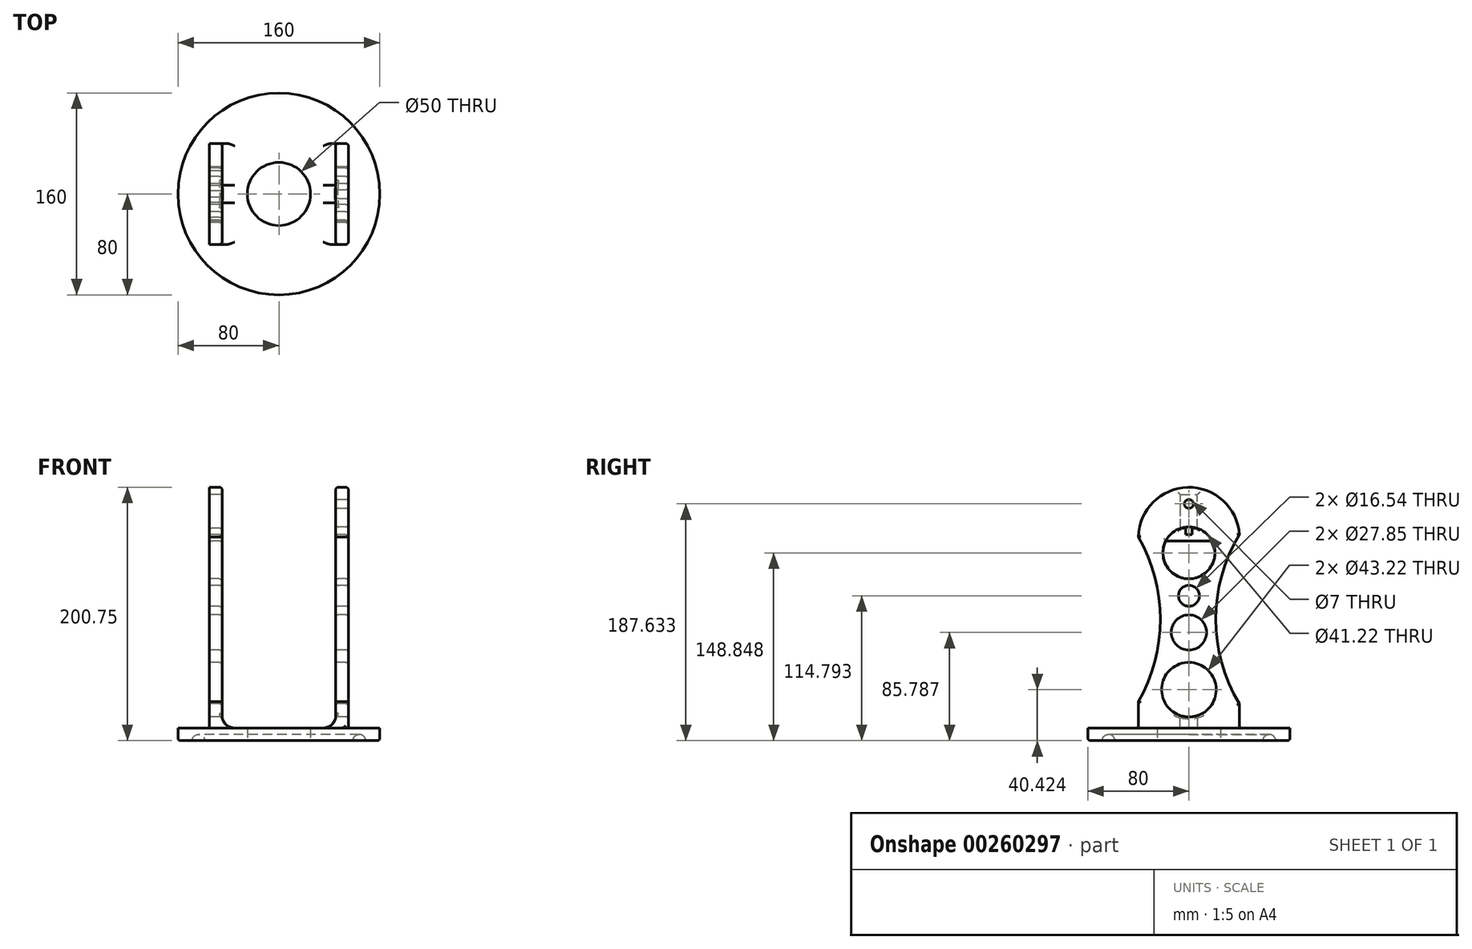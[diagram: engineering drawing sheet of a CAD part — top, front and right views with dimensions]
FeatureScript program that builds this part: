
annotation { "Feature Type Name" : "Feature", "Feature Type Description" : "" }
export const myFeature = defineFeature(function(context is Context, id is Id, definition is map)
    precondition{}
    {
        {
            var Q0;
            Q0=qCreatedBy(makeId("Top.planeOp"),FACE);
            var sketch = newSketch(context, id + "F0", { "sketchPlane" : qUnion([Q0])});
            skCircle(sketch, "E0", {"center": v(0, 0) * mm, "radius": 100 * mm});
            skSolve(sketch);
        }
        {
            var Q0;
            Q0=makeQuery(id+"F0.imprint","IMPRINT",FACE,{"disambiguationData":[TD([[makeQuery(id+"F0.imprint","IMPRINT",EDGE,{"derivedFrom":sQuery(id+"F0.wireOp",EDGE,"E0")}),1.0]])]});
            extrude(context, id + "F1", {"entities" : qUnion([Q0]), "depth" : 10 * mm});
        }
        {
            var Q0;
            Q0=qCreatedBy(makeId("Front.planeOp"),FACE);
            var sketch = newSketch(context, id + "F2", { "sketchPlane" : qUnion([Q0])});
            skCircle(sketch, "E1", {"center": v(-63.7, 0) * mm, "radius": 5 * mm});
            skLineSegment(sketch, "E2", {"start": v(0, 0) * mm, "end": v(-63.7, 0) * mm});
            skSolve(sketch);
        }
        {
            var Q0;
            Q0=makeQuery(id+"F2.imprint","IMPRINT",FACE,{"disambiguationData":[TD([[makeQuery(id+"F2.imprint","IMPRINT",EDGE,{"derivedFrom":sQuery(id+"F2.wireOp",EDGE,"E1")}),1.0]])]});
            var Q1;
            Q1=makeQuery(id+"F1.opExtrude","CAP_EDGE",EDGE,{"disambiguationData":[OSD([sQuery(id+"F0.wireOp",EDGE,"E0")])],"isStart":true});
            revolve(context, id + "F3", {"operationType" : NewBodyOperationType.REMOVE, "entities" : qUnion([Q0]), "axis" : qUnion([Q1]), "revolveType" : RevolveType.FULL, "oppositeDirection" : true});
        }
        {
            var Q0;
            Q0=makeQuery(id+"F1.opExtrude","CAP_FACE",FACE,{"disambiguationData":[OSD([sQuery(id+"F0.wireOp",EDGE,"E0")])],"isStart":false});
            cPlane(context, id + "F4", {"entities" : qUnion([Q0]), "cplaneType" : CPlaneType.OFFSET, "offset" : 0 * mm, "width" : 152.4 * mm, "height" : 152.4 * mm});
        }
        {
            var Q0;
            Q0=makeQuery(id+"F1.opExtrude","CAP_FACE",FACE,{"disambiguationData":[OSD([sQuery(id+"F0.wireOp",EDGE,"E0")])],"isStart":false});
            var sketch = newSketch(context, id + "F5", { "sketchPlane" : qUnion([Q0])});
            skLineSegment(sketch, "E3.bottom", {"start": v(55, 40) * mm, "end": v(-55, 40) * mm});
            skLineSegment(sketch, "E3.top", {"start": v(55, -40) * mm, "end": v(-55, -40) * mm});
            skLineSegment(sketch, "E3.left", {"start": v(55, 40) * mm, "end": v(55, -40) * mm});
            skLineSegment(sketch, "E3.right", {"start": v(-55, 40) * mm, "end": v(-55, -40) * mm});
            skPoint(sketch, "E3.middle", {"position": v(0, 0) * mm});
            skSolve(sketch);
        }
        {
            var Q0;
            Q0=makeQuery(id+"F5.imprint","IMPRINT",FACE,{"disambiguationData":[TD([[makeQuery(id+"F5.imprint","IMPRINT",EDGE,{"derivedFrom":sQuery(id+"F5.wireOp",EDGE,"E3.bottom")}),1.0]])]});
            extrude(context, id + "F6", {"entities" : qUnion([Q0]), "operationType" : NewBodyOperationType.ADD, "depth" : 195 * mm});
        }
        {
            var Q0;
            Q0=makeQuery(id+"F6.opExtrude","CAP_FACE",FACE,{"disambiguationData":[OSD([sQuery(id+"F5.wireOp",EDGE,"E3.bottom"),sQuery(id+"F5.wireOp",EDGE,"E3.top"),sQuery(id+"F5.wireOp",EDGE,"E3.left"),sQuery(id+"F5.wireOp",EDGE,"E3.right")])],"isStart":false});
            var sketch = newSketch(context, id + "F7", { "sketchPlane" : qUnion([Q0])});
            skLineSegment(sketch, "E4.bottom", {"start": v(45, 40) * mm, "end": v(-45, 40) * mm});
            skLineSegment(sketch, "E4.top", {"start": v(45, -40) * mm, "end": v(-45, -40) * mm});
            skLineSegment(sketch, "E4.left", {"start": v(45, 40) * mm, "end": v(45, -40) * mm});
            skLineSegment(sketch, "E4.right", {"start": v(-45, 40) * mm, "end": v(-45, -40) * mm});
            skPoint(sketch, "E4.middle", {"position": v(0, 0) * mm});
            skSolve(sketch);
        }
        {
            var Q0;
            Q0 = qSketchRegion(id + "F7", true);
            extrude(context, id + "F8", {"entities" : qUnion([Q0]), "operationType" : NewBodyOperationType.REMOVE, "oppositeDirection" : true, "depth" : 195 * mm});
        }
        {
            var Q0;
            Q0=qCreatedBy(makeId("Top.planeOp"),FACE);
            var sketch = newSketch(context, id + "F9", { "sketchPlane" : qUnion([Q0])});
            skCircle(sketch, "E5", {"center": v(0, 0) * mm, "radius": 3.75 * mm});
            skSolve(sketch);
        }
        {
            var Q0;
            Q0 = qSketchRegion(id + "F9", true);
            extrude(context, id + "F10", {"entities" : qUnion([Q0]), "operationType" : NewBodyOperationType.REMOVE, "depth" : 12 * mm});
        }
        {
            var Q0;
            Q0=makeQuery(id+"F3.boolean.opBoolean","SPLIT",FACE,{"disambiguationData":[TD([makeQuery(id+"F3.opRevolve","SWEPT_FACE",FACE,{"disambiguationData":[OSD([sQuery(id+"F2.wireOp",EDGE,"E1")])]})])],"derivedFrom":makeQuery(id+"F1.opExtrude","CAP_FACE",FACE,{"disambiguationData":[OSD([sQuery(id+"F0.wireOp",EDGE,"E0")])],"isStart":true})});
            var sketch = newSketch(context, id + "F11", { "sketchPlane" : qUnion([Q0])});
            skCircle(sketch, "E6", {"center": v(0, 0) * mm, "radius": 25 * mm});
            skSolve(sketch);
        }
        {
            var Q0;
            Q0 = qSketchRegion(id + "F11", true);
            extrude(context, id + "F12", {"entities" : qUnion([Q0]), "operationType" : NewBodyOperationType.REMOVE, "oppositeDirection" : true, "depth" : 16 * mm});
        }
        {
            var Q0;
            Q0=makeQuery(id+"F6.opExtrude","SWEPT_FACE",FACE,{"disambiguationData":[OSD([sQuery(id+"F5.wireOp",EDGE,"E3.left")])]});
            var sketch = newSketch(context, id + "F13", { "sketchPlane" : qUnion([Q0])});
            skCircle(sketch, "E7", {"center": v(0, 187.63) * mm, "radius": 3.5 * mm});
            skPoint(sketch, "E7.centerSnap0", {"position": v(0, 195) * mm});
            skSolve(sketch);
        }
        {
            var Q0;
            Q0 = qSketchRegion(id + "F13", true);
            extrude(context, id + "F14", {"entities" : qUnion([Q0]), "operationType" : NewBodyOperationType.REMOVE, "oppositeDirection" : true, "depth" : 123.95 * mm});
        }
        {
            var Q0;
            Q0=makeQuery(id+"F3.boolean.opBoolean","INTERSECT",EDGE,{"disambiguationData":[OD(0.0)],"derivedFrom":[makeQuery(id+"F1.opExtrude","CAP_FACE",FACE,{"disambiguationData":[OSD([sQuery(id+"F0.wireOp",EDGE,"E0")])],"isStart":true}),makeQuery(id+"F3.opRevolve","SWEPT_FACE",FACE,{"disambiguationData":[OSD([sQuery(id+"F2.wireOp",EDGE,"E1")])]})]});
            var Q1;
            Q1=makeQuery(id+"F3.boolean.opBoolean","INTERSECT",EDGE,{"disambiguationData":[OD(1.0)],"derivedFrom":[makeQuery(id+"F1.opExtrude","CAP_FACE",FACE,{"disambiguationData":[OSD([sQuery(id+"F0.wireOp",EDGE,"E0")])],"isStart":true}),makeQuery(id+"F3.opRevolve","SWEPT_FACE",FACE,{"disambiguationData":[OSD([sQuery(id+"F2.wireOp",EDGE,"E1")])]})]});
            fillet(context, id + "F15", {"entities" : qUnion([Q0, Q1]), "radius" : 2 * mm, "tangentPropagation" : true, "allowEdgeOverflow" : false});
        }
        {
            var Q0;
            Q0=makeQuery(id+"F6.opExtrude","SWEPT_FACE",FACE,{"disambiguationData":[OSD([sQuery(id+"F5.wireOp",EDGE,"E3.right")])]});
            var sketch = newSketch(context, id + "F16", { "sketchPlane" : qUnion([Q0])});
            skArc(sketch, "E8", {"start": v(40, 161.53) * mm, "mid": v(0.84, 200.74) * mm, "end": v(-40, 163.27) * mm});
            skArc(sketch, "E9", {"start": v(-40, 29.22) * mm, "mid": v(-21.31, 96.25) * mm, "end": v(-40, 163.27) * mm});
            skArc(sketch, "E10", {"start": v(40, 161.53) * mm, "mid": v(22.68, 96.23) * mm, "end": v(40, 30.93) * mm});
            skSolve(sketch);
        }
        {
            var Q0;
            {var subQ0=sQuery(id+"F16.wireOp",EDGE,"E8");var subQ1=sQuery(id+"F5.wireOp",EDGE,"E3.right");var subQ4=makeQuery(id+"F6.opExtrude","CAP_EDGE",EDGE,{"disambiguationData":[OSD([subQ1])],"isStart":false});var subQ5=makeQuery(id+"F16.imprint","INTERSECT",VERTEX,{"disambiguationData":[OD(1.0)],"derivedFrom":[subQ4,subQ0]});Q0=makeQuery(id+"F16.imprint","IMPRINT",FACE,{"disambiguationData":[TD([[makeQuery(id+"F16.imprint","IMPRINT",EDGE,{"disambiguationData":[TD([[subQ5,1.0]])],"derivedFrom":subQ4}),-1.0]])]});}
            var Q1;
            {var subQ0=sQuery(id+"F16.wireOp",EDGE,"E8");var subQ1=sQuery(id+"F5.wireOp",EDGE,"E3.right");var subQ4=makeQuery(id+"F6.opExtrude","CAP_EDGE",EDGE,{"disambiguationData":[OSD([subQ1])],"isStart":false});var subQ5=makeQuery(id+"F16.imprint","INTERSECT",VERTEX,{"disambiguationData":[OD(0.0)],"derivedFrom":[subQ4,subQ0]});Q1=makeQuery(id+"F16.imprint","IMPRINT",FACE,{"disambiguationData":[TD([[makeQuery(id+"F16.imprint","IMPRINT",EDGE,{"disambiguationData":[TD([[subQ5,-1.0]])],"derivedFrom":subQ4}),-1.0]])]});}
            var Q2;
            {var subQ0=sQuery(id+"F16.wireOp",EDGE,"E10");Q2=makeQuery(id+"F16.imprint","IMPRINT",FACE,{"disambiguationData":[TD([[makeQuery(id+"F16.imprint","IMPRINT",EDGE,{"derivedFrom":subQ0}),1.0]])]});}
            var Q3;
            {var subQ0=sQuery(id+"F16.wireOp",EDGE,"E9");Q3=makeQuery(id+"F16.imprint","IMPRINT",FACE,{"disambiguationData":[TD([[makeQuery(id+"F16.imprint","IMPRINT",EDGE,{"derivedFrom":subQ0}),1.0]])]});}
            extrude(context, id + "F17", {"entities" : qUnion([Q0, Q1, Q2, Q3]), "operationType" : NewBodyOperationType.REMOVE, "oppositeDirection" : true, "depth" : 124.97 * mm});
        }
        {
            var Q0;
            Q0=makeQuery(id+"F6.opExtrude","SWEPT_FACE",FACE,{"disambiguationData":[OSD([sQuery(id+"F5.wireOp",EDGE,"E3.right")])]});
            var sketch = newSketch(context, id + "F18", { "sketchPlane" : qUnion([Q0])});
            skCircle(sketch, "E11", {"center": v(0, 148.85) * mm, "radius": 20.6 * mm});
            skCircle(sketch, "E12", {"center": v(0, 40.42) * mm, "radius": 21.6 * mm});
            skCircle(sketch, "E13", {"center": v(0, 85.79) * mm, "radius": 13.93 * mm});
            skCircle(sketch, "E14", {"center": v(0, 114.8) * mm, "radius": 8.27 * mm});
            skSolve(sketch);
        }
        {
            var Q0;
            Q0 = qSketchRegion(id + "F18", true);
            extrude(context, id + "F19", {"entities" : qUnion([Q0]), "operationType" : NewBodyOperationType.REMOVE, "oppositeDirection" : true, "depth" : 123.44 * mm});
        }
        {
            var Q0;
            Q0=makeQuery(id+"F6.opExtrude","SWEPT_FACE",FACE,{"disambiguationData":[OSD([sQuery(id+"F5.wireOp",EDGE,"E3.right")])]});
            var sketch = newSketch(context, id + "F20", { "sketchPlane" : qUnion([Q0])});
            skLineSegment(sketch, "E15.bottom", {"start": v(6.7, 180.33) * mm, "end": v(-6.7, 180.33) * mm});
            skLineSegment(sketch, "E15.top", {"start": v(6.7, 194.93) * mm, "end": v(-6.7, 194.93) * mm});
            skLineSegment(sketch, "E15.left", {"start": v(6.7, 180.33) * mm, "end": v(6.7, 194.93) * mm});
            skLineSegment(sketch, "E15.right", {"start": v(-6.7, 180.33) * mm, "end": v(-6.7, 194.93) * mm});
            skPoint(sketch, "E15.middle", {"position": v(0, 187.63) * mm});
            skLineSegment(sketch, "E16", {"start": v(-6.7, 180.33) * mm, "end": v(-6.7, 168.34) * mm});
            skLineSegment(sketch, "E17", {"start": v(-6.7, 168.34) * mm, "end": v(6.7, 168.34) * mm});
            skLineSegment(sketch, "E18", {"start": v(6.7, 168.34) * mm, "end": v(6.7, 180.33) * mm});
            skSolve(sketch);
        }
        {
            var Q0;
            Q0=makeQuery(id+"F20.imprint","IMPRINT",FACE,{"disambiguationData":[TD([[makeQuery(id+"F20.imprint","IMPRINT",EDGE,{"derivedFrom":sQuery(id+"F20.wireOp",EDGE,"E15.bottom")}),-1.0]])]});
            var Q1;
            Q1=makeQuery(id+"F20.imprint","IMPRINT",FACE,{"disambiguationData":[TD([[makeQuery(id+"F20.imprint","IMPRINT",EDGE,{"derivedFrom":sQuery(id+"F20.wireOp",EDGE,"E15.bottom")}),1.0]])]});
            extrude(context, id + "F21", {"entities" : qUnion([Q0, Q1]), "operationType" : NewBodyOperationType.REMOVE, "oppositeDirection" : true, "depth" : 11 * mm});
        }
        {
            var Q0;
            Q0=makeQuery(id+"F6.opExtrude","SWEPT_FACE",FACE,{"disambiguationData":[OSD([sQuery(id+"F5.wireOp",EDGE,"E3.right")])]});
            var sketch = newSketch(context, id + "F22", { "sketchPlane" : qUnion([Q0])});
            skLineSegment(sketch, "E19", {"start": v(-6.7, 168.34) * mm, "end": v(6.7, 168.34) * mm});
            skLineSegment(sketch, "E20", {"start": v(-18.4, 158.14) * mm, "end": v(18.4, 158.14) * mm});
            skSolve(sketch);
        }
        {
            var Q0;
            {var subQ0=sQuery(id+"F22.wireOp",EDGE,"E19");Q0=makeQuery(id+"F22.imprint","IMPRINT",FACE,{"disambiguationData":[TD([[makeQuery(id+"F22.imprint","IMPRINT",EDGE,{"derivedFrom":subQ0}),-1.0]])]});}
            extrude(context, id + "F23", {"entities" : qUnion([Q0]), "operationType" : NewBodyOperationType.ADD, "oppositeDirection" : true, "depth" : 10 * mm});
        }
        {
            var Q0;
            {var subQ0=sQuery(id+"FvlRTXBBaTxduJt_1.wireOp",EDGE,"E7vVl7CL-9N4T-M4Wq-ayos-x9gGrK3uOBEP.right");var subQ1=sQuery(id+"FvlRTXBBaTxduJt_1.wireOp",EDGE,"E7vVl7CL-9N4T-M4Wq-ayos-x9gGrK3uOBEP.left");var subQ2=sQuery(id+"FvlRTXBBaTxduJt_1.wireOp",EDGE,"E7vVl7CL-9N4T-M4Wq-ayos-x9gGrK3uOBEP.top");var subQ3=sQuery(id+"FvlRTXBBaTxduJt_1.wireOp",EDGE,"E7vVl7CL-9N4T-M4Wq-ayos-x9gGrK3uOBEP.bottom");Q0=makeQuery(id+"FjyFYaAjEJBvV5w_1.1.FbtMya7PSzrZqRG_1.boolean.opBoolean","MERGE",FACE,{"derivedFrom":[makeQuery(id+"FbtMya7PSzrZqRG_1.boolean.opBoolean","MERGE",FACE,{"derivedFrom":[makeQuery(id+"FokIs1tahE0cSG3_1.opPattern","SPLIT",FACE,{"disambiguationData":[OD(8.0)],"derivedFrom":makeQuery(id+"F8.boolean.opBoolean","MERGE",FACE,{"derivedFrom":[makeQuery(id+"F1.opExtrude","CAP_FACE",FACE,{"disambiguationData":[OSD([sQuery(id+"F0.wireOp",EDGE,"E0")])],"isStart":false}),makeQuery(id+"F8.opExtrude","CAP_FACE",FACE,{"disambiguationData":[OSD([sQuery(id+"F7.wireOp",EDGE,"E4.bottom"),sQuery(id+"F7.wireOp",EDGE,"E4.top"),sQuery(id+"F7.wireOp",EDGE,"E4.left"),sQuery(id+"F7.wireOp",EDGE,"E4.right")])],"isStart":false})]})}),makeQuery(id+"FbtMya7PSzrZqRG_1.opExtrude","CAP_FACE",FACE,{"disambiguationData":[OSD([subQ3,subQ2,subQ1,subQ0])],"isStart":false})]}),makeQuery(id+"FjyFYaAjEJBvV5w_1.1.FbtMya7PSzrZqRG_1.opExtrude","CAP_FACE",FACE,{"disambiguationData":[OSD([subQ3,subQ2,subQ1,subQ0])],"isStart":false})]});}
            var sketch = newSketch(context, id + "F24", { "sketchPlane" : qUnion([Q0])});
            skCircle(sketch, "E21", {"center": v(0, 0) * mm, "radius": 80 * mm});
            skCircle(sketch, "E22", {"center": v(0, 0) * mm, "radius": 100 * mm});
            skSolve(sketch);
        }
        {
            var Q0;
            Q0 = qSketchRegion(id + "F24", true);
            extrude(context, id + "F25", {"entities" : qUnion([Q0]), "operationType" : NewBodyOperationType.REMOVE, "oppositeDirection" : true, "depth" : 11 * mm});
        }
        {
            var Q0;
            {var subQ0=makeQuery(id+"F6.opExtrude","CAP_EDGE",EDGE,{"disambiguationData":[OSD([sQuery(id+"F5.wireOp",EDGE,"E3.left")])],"isStart":true});Q0=makeQuery(id+"FjyFYaAjEJBvV5w_1.1.FbtMya7PSzrZqRG_1.boolean.opBoolean","MERGE",EDGE,{"derivedFrom":[makeQuery(id+"FokIs1tahE0cSG3_1.opPattern","SPLIT",EDGE,{"disambiguationData":[OD(0.0)],"derivedFrom":subQ0}),makeQuery(id+"FokIs1tahE0cSG3_1.opPattern","SPLIT",EDGE,{"disambiguationData":[OD(1.0)],"derivedFrom":subQ0}),makeQuery(id+"FokIs1tahE0cSG3_1.opPattern","SPLIT",EDGE,{"disambiguationData":[OD(2.0)],"derivedFrom":subQ0}),makeQuery(id+"FokIs1tahE0cSG3_1.opPattern","SPLIT",EDGE,{"disambiguationData":[OD(3.0)],"derivedFrom":subQ0}),makeQuery(id+"FokIs1tahE0cSG3_1.opPattern","SPLIT",EDGE,{"disambiguationData":[OD(4.0)],"derivedFrom":subQ0})]});}
            var Q1;
            {var subQ0=makeQuery(id+"F6.opExtrude","CAP_EDGE",EDGE,{"disambiguationData":[OSD([sQuery(id+"F5.wireOp",EDGE,"E3.right")])],"isStart":true});Q1=makeQuery(id+"FbtMya7PSzrZqRG_1.boolean.opBoolean","MERGE",EDGE,{"derivedFrom":[makeQuery(id+"FokIs1tahE0cSG3_1.opPattern","SPLIT",EDGE,{"disambiguationData":[OD(0.0)],"derivedFrom":subQ0}),makeQuery(id+"FokIs1tahE0cSG3_1.opPattern","SPLIT",EDGE,{"disambiguationData":[OD(1.0)],"derivedFrom":subQ0}),makeQuery(id+"FokIs1tahE0cSG3_1.opPattern","SPLIT",EDGE,{"disambiguationData":[OD(2.0)],"derivedFrom":subQ0}),makeQuery(id+"FokIs1tahE0cSG3_1.opPattern","SPLIT",EDGE,{"disambiguationData":[OD(3.0)],"derivedFrom":subQ0}),makeQuery(id+"FokIs1tahE0cSG3_1.opPattern","SPLIT",EDGE,{"disambiguationData":[OD(4.0)],"derivedFrom":subQ0})]});}
            var Q2;
            Q2=makeQuery(id+"F8.boolean.opBoolean","COPY",EDGE,{"derivedFrom":makeQuery(id+"F8.opExtrude","CAP_EDGE",EDGE,{"disambiguationData":[OSD([sQuery(id+"F7.wireOp",EDGE,"E4.right")])],"isStart":false})});
            var Q3;
            {var subQ1=sQuery(id+"F5.wireOp",EDGE,"E3.bottom");Q3=makeQuery(id+"F8.boolean.opBoolean","SPLIT",EDGE,{"disambiguationData":[TD([makeQuery(id+"F6.opExtrude","SWEPT_FACE",FACE,{"disambiguationData":[OSD([sQuery(id+"F5.wireOp",EDGE,"E3.right")])]})])],"derivedFrom":makeQuery(id+"F6.opExtrude","CAP_EDGE",EDGE,{"disambiguationData":[OSD([subQ1])],"isStart":true})});}
            var Q4;
            {var subQ1=sQuery(id+"F5.wireOp",EDGE,"E3.bottom");Q4=makeQuery(id+"F8.boolean.opBoolean","SPLIT",EDGE,{"disambiguationData":[TD([makeQuery(id+"F6.opExtrude","SWEPT_FACE",FACE,{"disambiguationData":[OSD([sQuery(id+"F5.wireOp",EDGE,"E3.left")])]})])],"derivedFrom":makeQuery(id+"F6.opExtrude","CAP_EDGE",EDGE,{"disambiguationData":[OSD([subQ1])],"isStart":true})});}
            var Q5;
            Q5=makeQuery(id+"F8.boolean.opBoolean","COPY",EDGE,{"derivedFrom":makeQuery(id+"F8.opExtrude","CAP_EDGE",EDGE,{"disambiguationData":[OSD([sQuery(id+"F7.wireOp",EDGE,"E4.left")])],"isStart":false})});
            var Q6;
            {var subQ1=sQuery(id+"F5.wireOp",EDGE,"E3.top");Q6=makeQuery(id+"F8.boolean.opBoolean","SPLIT",EDGE,{"disambiguationData":[TD([makeQuery(id+"F6.opExtrude","SWEPT_FACE",FACE,{"disambiguationData":[OSD([sQuery(id+"F5.wireOp",EDGE,"E3.right")])]})])],"derivedFrom":makeQuery(id+"F6.opExtrude","CAP_EDGE",EDGE,{"disambiguationData":[OSD([subQ1])],"isStart":true})});}
            var Q7;
            {var subQ1=sQuery(id+"F5.wireOp",EDGE,"E3.top");Q7=makeQuery(id+"F8.boolean.opBoolean","SPLIT",EDGE,{"disambiguationData":[TD([makeQuery(id+"F6.opExtrude","SWEPT_FACE",FACE,{"disambiguationData":[OSD([sQuery(id+"F5.wireOp",EDGE,"E3.left")])]})])],"derivedFrom":makeQuery(id+"F6.opExtrude","CAP_EDGE",EDGE,{"disambiguationData":[OSD([subQ1])],"isStart":true})});}
            fillet(context, id + "F26", {"entities" : qUnion([Q0, Q1, Q2, Q3, Q4, Q5, Q6, Q7]), "radius" : 10 * mm, "tangentPropagation" : true, "allowEdgeOverflow" : false});
        }
        {
            var Q0;
            Q0=makeQuery(id+"F8.boolean.opBoolean","COPY",FACE,{"derivedFrom":makeQuery(id+"F8.opExtrude","SWEPT_FACE",FACE,{"disambiguationData":[OSD([sQuery(id+"F7.wireOp",EDGE,"E4.left")])]})});
            var Q1;
            Q1=makeQuery(id+"F6.opExtrude","SWEPT_FACE",FACE,{"disambiguationData":[OSD([sQuery(id+"F5.wireOp",EDGE,"E3.left")])]});
            var Q2;
            Q2=makeQuery(id+"F23.boolean.opBoolean","MERGE",FACE,{"derivedFrom":[makeQuery(id+"F8.boolean.opBoolean","COPY",FACE,{"derivedFrom":makeQuery(id+"F8.opExtrude","SWEPT_FACE",FACE,{"disambiguationData":[OSD([sQuery(id+"F7.wireOp",EDGE,"E4.right")])]})}),makeQuery(id+"F23.opExtrude","CAP_FACE",FACE,{"disambiguationData":[OSD([sQuery(id+"F18.wireOp",EDGE,"E11"),sQuery(id+"F22.wireOp",EDGE,"E19"),sQuery(id+"F22.wireOp",EDGE,"E20")])],"isStart":false})]});
            var Q3;
            Q3=makeQuery(id+"F19.boolean.opBoolean","COPY",EDGE,{"derivedFrom":makeQuery(id+"F19.opExtrude","CAP_EDGE",EDGE,{"disambiguationData":[OSD([sQuery(id+"F18.wireOp",EDGE,"E12")])],"isStart":true})});
            var Q4;
            {var subQ0=sQuery(id+"F5.wireOp",EDGE,"E3.left");Q4=makeQuery(id+"F26.opFillet","BLEND_EDGE",EDGE,{"blendedFrom":[makeQuery(id+"F6.opExtrude","CAP_EDGE",EDGE,{"disambiguationData":[OSD([subQ0])],"isStart":true}),makeQuery(id+"F19.boolean.opBoolean","COPY",FACE,{"disambiguationData":[TD([makeQuery(id+"F6.opExtrude","SWEPT_FACE",FACE,{"disambiguationData":[OSD([subQ0])]})])],"derivedFrom":makeQuery(id+"F19.opExtrude","SWEPT_FACE",FACE,{"disambiguationData":[OSD([sQuery(id+"F18.wireOp",EDGE,"E12")])]})})],"blendedInto":[makeQuery(id+"F19.boolean.opBoolean","COPY",FACE,{"disambiguationData":[TD([makeQuery(id+"F6.opExtrude","SWEPT_FACE",FACE,{"disambiguationData":[OSD([subQ0])]})])],"derivedFrom":makeQuery(id+"F19.opExtrude","SWEPT_FACE",FACE,{"disambiguationData":[OSD([sQuery(id+"F18.wireOp",EDGE,"E12")])]})})]});}
            var Q5;
            {var subQ0=sQuery(id+"F5.wireOp",EDGE,"E3.right");Q5=makeQuery(id+"F26.opFillet","BLEND_EDGE",EDGE,{"blendedFrom":[makeQuery(id+"F6.opExtrude","CAP_EDGE",EDGE,{"disambiguationData":[OSD([subQ0])],"isStart":true}),makeQuery(id+"F19.boolean.opBoolean","COPY",FACE,{"disambiguationData":[TD([makeQuery(id+"F6.opExtrude","SWEPT_FACE",FACE,{"disambiguationData":[OSD([subQ0])]})])],"derivedFrom":makeQuery(id+"F19.opExtrude","SWEPT_FACE",FACE,{"disambiguationData":[OSD([sQuery(id+"F18.wireOp",EDGE,"E12")])]})})],"blendedInto":[makeQuery(id+"F19.boolean.opBoolean","COPY",FACE,{"disambiguationData":[TD([makeQuery(id+"F6.opExtrude","SWEPT_FACE",FACE,{"disambiguationData":[OSD([subQ0])]})])],"derivedFrom":makeQuery(id+"F19.opExtrude","SWEPT_FACE",FACE,{"disambiguationData":[OSD([sQuery(id+"F18.wireOp",EDGE,"E12")])]})})]});}
            var Q6;
            {var subQ0=sQuery(id+"F7.wireOp",EDGE,"E4.right");Q6=makeQuery(id+"F26.opFillet","BLEND_EDGE",EDGE,{"blendedFrom":[makeQuery(id+"F8.boolean.opBoolean","COPY",EDGE,{"derivedFrom":makeQuery(id+"F8.opExtrude","CAP_EDGE",EDGE,{"disambiguationData":[OSD([subQ0])],"isStart":false})}),makeQuery(id+"F19.boolean.opBoolean","COPY",FACE,{"disambiguationData":[TD([makeQuery(id+"F6.opExtrude","SWEPT_FACE",FACE,{"disambiguationData":[OSD([sQuery(id+"F5.wireOp",EDGE,"E3.right")])]})])],"derivedFrom":makeQuery(id+"F19.opExtrude","SWEPT_FACE",FACE,{"disambiguationData":[OSD([sQuery(id+"F18.wireOp",EDGE,"E12")])]})})],"blendedInto":[makeQuery(id+"F19.boolean.opBoolean","COPY",FACE,{"disambiguationData":[TD([makeQuery(id+"F6.opExtrude","SWEPT_FACE",FACE,{"disambiguationData":[OSD([sQuery(id+"F5.wireOp",EDGE,"E3.right")])]})])],"derivedFrom":makeQuery(id+"F19.opExtrude","SWEPT_FACE",FACE,{"disambiguationData":[OSD([sQuery(id+"F18.wireOp",EDGE,"E12")])]})})]});}
            var Q7;
            {var subQ0=sQuery(id+"F7.wireOp",EDGE,"E4.left");Q7=makeQuery(id+"F26.opFillet","BLEND_EDGE",EDGE,{"blendedFrom":[makeQuery(id+"F8.boolean.opBoolean","COPY",EDGE,{"derivedFrom":makeQuery(id+"F8.opExtrude","CAP_EDGE",EDGE,{"disambiguationData":[OSD([subQ0])],"isStart":false})}),makeQuery(id+"F19.boolean.opBoolean","COPY",FACE,{"disambiguationData":[TD([makeQuery(id+"F6.opExtrude","SWEPT_FACE",FACE,{"disambiguationData":[OSD([sQuery(id+"F5.wireOp",EDGE,"E3.left")])]})])],"derivedFrom":makeQuery(id+"F19.opExtrude","SWEPT_FACE",FACE,{"disambiguationData":[OSD([sQuery(id+"F18.wireOp",EDGE,"E12")])]})})],"blendedInto":[makeQuery(id+"F19.boolean.opBoolean","COPY",FACE,{"disambiguationData":[TD([makeQuery(id+"F6.opExtrude","SWEPT_FACE",FACE,{"disambiguationData":[OSD([sQuery(id+"F5.wireOp",EDGE,"E3.left")])]})])],"derivedFrom":makeQuery(id+"F19.opExtrude","SWEPT_FACE",FACE,{"disambiguationData":[OSD([sQuery(id+"F18.wireOp",EDGE,"E12")])]})})]});}
            var Q8;
            Q8=makeQuery(id+"F17.boolean.opBoolean","COPY",EDGE,{"derivedFrom":makeQuery(id+"F17.opExtrude","CAP_EDGE",EDGE,{"disambiguationData":[OSD([sQuery(id+"F16.wireOp",EDGE,"E8")])],"isStart":true})});
            var Q9;
            Q9=makeQuery(id+"F17.boolean.opBoolean","COPY",EDGE,{"derivedFrom":makeQuery(id+"F17.opExtrude","CAP_EDGE",EDGE,{"disambiguationData":[OSD([sQuery(id+"F16.wireOp",EDGE,"E10")])],"isStart":true})});
            var Q10;
            Q10=makeQuery(id+"F17.boolean.opBoolean","COPY",EDGE,{"derivedFrom":makeQuery(id+"F17.opExtrude","CAP_EDGE",EDGE,{"disambiguationData":[OSD([sQuery(id+"F16.wireOp",EDGE,"E9")])],"isStart":true})});
            var Q11;
            Q11=makeQuery(id+"F19.boolean.opBoolean","COPY",EDGE,{"derivedFrom":makeQuery(id+"F19.opExtrude","CAP_EDGE",EDGE,{"disambiguationData":[OSD([sQuery(id+"F18.wireOp",EDGE,"E11")])],"isStart":true})});
            var Q12;
            Q12=makeQuery(id+"F19.boolean.opBoolean","COPY",EDGE,{"derivedFrom":makeQuery(id+"F19.opExtrude","CAP_EDGE",EDGE,{"disambiguationData":[OSD([sQuery(id+"F18.wireOp",EDGE,"E14")])],"isStart":true})});
            var Q13;
            Q13=makeQuery(id+"F19.boolean.opBoolean","COPY",EDGE,{"derivedFrom":makeQuery(id+"F19.opExtrude","CAP_EDGE",EDGE,{"disambiguationData":[OSD([sQuery(id+"F18.wireOp",EDGE,"E13")])],"isStart":true})});
            var Q14;
            Q14=makeQuery(id+"F21.boolean.opBoolean","COPY",EDGE,{"derivedFrom":makeQuery(id+"F21.opExtrude","CAP_EDGE",EDGE,{"disambiguationData":[OSD([sQuery(id+"F20.wireOp",EDGE,"E15.right"),sQuery(id+"F20.wireOp",EDGE,"E16")])],"isStart":true})});
            var Q15;
            Q15=makeQuery(id+"F21.boolean.opBoolean","COPY",EDGE,{"derivedFrom":makeQuery(id+"F21.opExtrude","CAP_EDGE",EDGE,{"disambiguationData":[OSD([sQuery(id+"F20.wireOp",EDGE,"E15.top")])],"isStart":true})});
            var Q16;
            Q16=makeQuery(id+"F21.boolean.opBoolean","COPY",EDGE,{"derivedFrom":makeQuery(id+"F21.opExtrude","CAP_EDGE",EDGE,{"disambiguationData":[OSD([sQuery(id+"F20.wireOp",EDGE,"E15.left"),sQuery(id+"F20.wireOp",EDGE,"E18")])],"isStart":true})});
            var Q17;
            Q17=makeQuery(id+"F23.opExtrude","CAP_EDGE",EDGE,{"disambiguationData":[OSD([sQuery(id+"F22.wireOp",EDGE,"E20")])],"isStart":true});
            var Q18;
            {var subQ0=sQuery(id+"F0.wireOp",EDGE,"E0");Q18=makeQuery(id+"F25.boolean.opBoolean","INTERSECT",EDGE,{"derivedFrom":[makeQuery(id+"F3.boolean.opBoolean","SPLIT",FACE,{"disambiguationData":[TD([makeQuery(id+"F1.opExtrude","SWEPT_FACE",FACE,{"disambiguationData":[OSD([subQ0])]}),makeQuery(id+"F3.opRevolve","SWEPT_FACE",FACE,{"disambiguationData":[OSD([sQuery(id+"F2.wireOp",EDGE,"E1")])]})])],"derivedFrom":makeQuery(id+"F1.opExtrude","CAP_FACE",FACE,{"disambiguationData":[OSD([subQ0])],"isStart":true})}),makeQuery(id+"F25.opExtrude","SWEPT_FACE",FACE,{"disambiguationData":[OSD([sQuery(id+"F24.wireOp",EDGE,"E21")])]})]});}
            var Q19;
            Q19=makeQuery(id+"F25.boolean.opBoolean","COPY",EDGE,{"derivedFrom":makeQuery(id+"F25.opExtrude","CAP_EDGE",EDGE,{"disambiguationData":[OSD([sQuery(id+"F24.wireOp",EDGE,"E21")])],"isStart":true})});
            var Q20;
            Q20=makeQuery(id+"F25.boolean.opBoolean","COPY",EDGE,{"derivedFrom":makeQuery(id+"F25.opExtrude","CAP_EDGE",EDGE,{"disambiguationData":[OSD([sQuery(id+"F24.wireOp",EDGE,"E21")])],"isStart":true})});
            var Q21;
            Q21=makeQuery(id+"F25.boolean.opBoolean","COPY",EDGE,{"derivedFrom":makeQuery(id+"F25.opExtrude","CAP_EDGE",EDGE,{"disambiguationData":[OSD([sQuery(id+"F24.wireOp",EDGE,"E21")])],"isStart":true})});
            var Q22;
            Q22=makeQuery(id+"F25.boolean.opBoolean","COPY",EDGE,{"derivedFrom":makeQuery(id+"F25.opExtrude","CAP_EDGE",EDGE,{"disambiguationData":[OSD([sQuery(id+"F24.wireOp",EDGE,"E21")])],"isStart":true})});
            var Q23;
            Q23=makeQuery(id+"F23.opExtrude","CAP_EDGE",EDGE,{"disambiguationData":[OSD([sQuery(id+"F22.wireOp",EDGE,"E19")])],"isStart":true});
            fillet(context, id + "F27", {"entities" : qUnion([Q0, Q1, Q2, Q3, Q4, Q5, Q6, Q7, Q8, Q9, Q10, Q11, Q12, Q13, Q14, Q15, Q16, Q17, Q18, Q19, Q20, Q21, Q22, Q23]), "radius" : 2 * mm, "tangentPropagation" : true, "allowEdgeOverflow" : false});
        }
        {
            var Q0;
            Q0=makeQuery(id+"F23.boolean.opBoolean","MERGE",FACE,{"derivedFrom":[makeQuery(id+"F6.opExtrude","SWEPT_FACE",FACE,{"disambiguationData":[OSD([sQuery(id+"F5.wireOp",EDGE,"E3.right")])]}),makeQuery(id+"F23.opExtrude","CAP_FACE",FACE,{"disambiguationData":[OSD([sQuery(id+"F18.wireOp",EDGE,"E11"),sQuery(id+"F22.wireOp",EDGE,"E19"),sQuery(id+"F22.wireOp",EDGE,"E20")])],"isStart":true})]});
            var sketch = newSketch(context, id + "F28", { "sketchPlane" : qUnion([Q0])});
            skLineSegment(sketch, "E23.bottom", {"start": v(2.5, 163.34) * mm, "end": v(-2.5, 163.34) * mm});
            skLineSegment(sketch, "E23.top", {"start": v(2.5, 173.34) * mm, "end": v(-2.5, 173.34) * mm});
            skLineSegment(sketch, "E23.left", {"start": v(2.5, 163.34) * mm, "end": v(2.5, 173.34) * mm});
            skLineSegment(sketch, "E23.right", {"start": v(-2.5, 163.34) * mm, "end": v(-2.5, 173.34) * mm});
            skPoint(sketch, "E23.middle", {"position": v(0, 168.34) * mm});
            skSolve(sketch);
        }
        {
            var Q0;
            Q0 = qSketchRegion(id + "F28", true);
            extrude(context, id + "F29", {"entities" : qUnion([Q0]), "operationType" : NewBodyOperationType.REMOVE, "oppositeDirection" : true, "depth" : 25.4 * mm});
        }
    });
